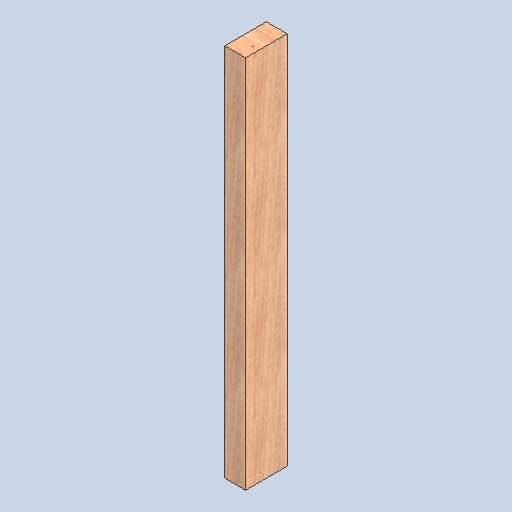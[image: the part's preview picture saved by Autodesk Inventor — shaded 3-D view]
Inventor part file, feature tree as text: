
AUTODESK INVENTOR PART (.ipt)
format: ipt  version: 2025 (Build 290162000, 162)  size: 148,992 bytes
history: native  units: in
note: dims shown in document units (in); Inventor stores cm internally (conversion verified against a paired STEP export)
features: other x3, sketch x1
ambient origin geometry x8: Origin, YZ Plane, XZ Plane, XY Plane, X Axis, Y Axis, Z Axis, Center Point
bodies: Solid1 (feature_tree)
feature tree (4):
  other  "2x4x36.ipt"
  other  "Solid1::2x4x36.ipt"
  other  "TaggingFeature1"
  sketch  "Sketch1"  dims[d0=0.3937in]
